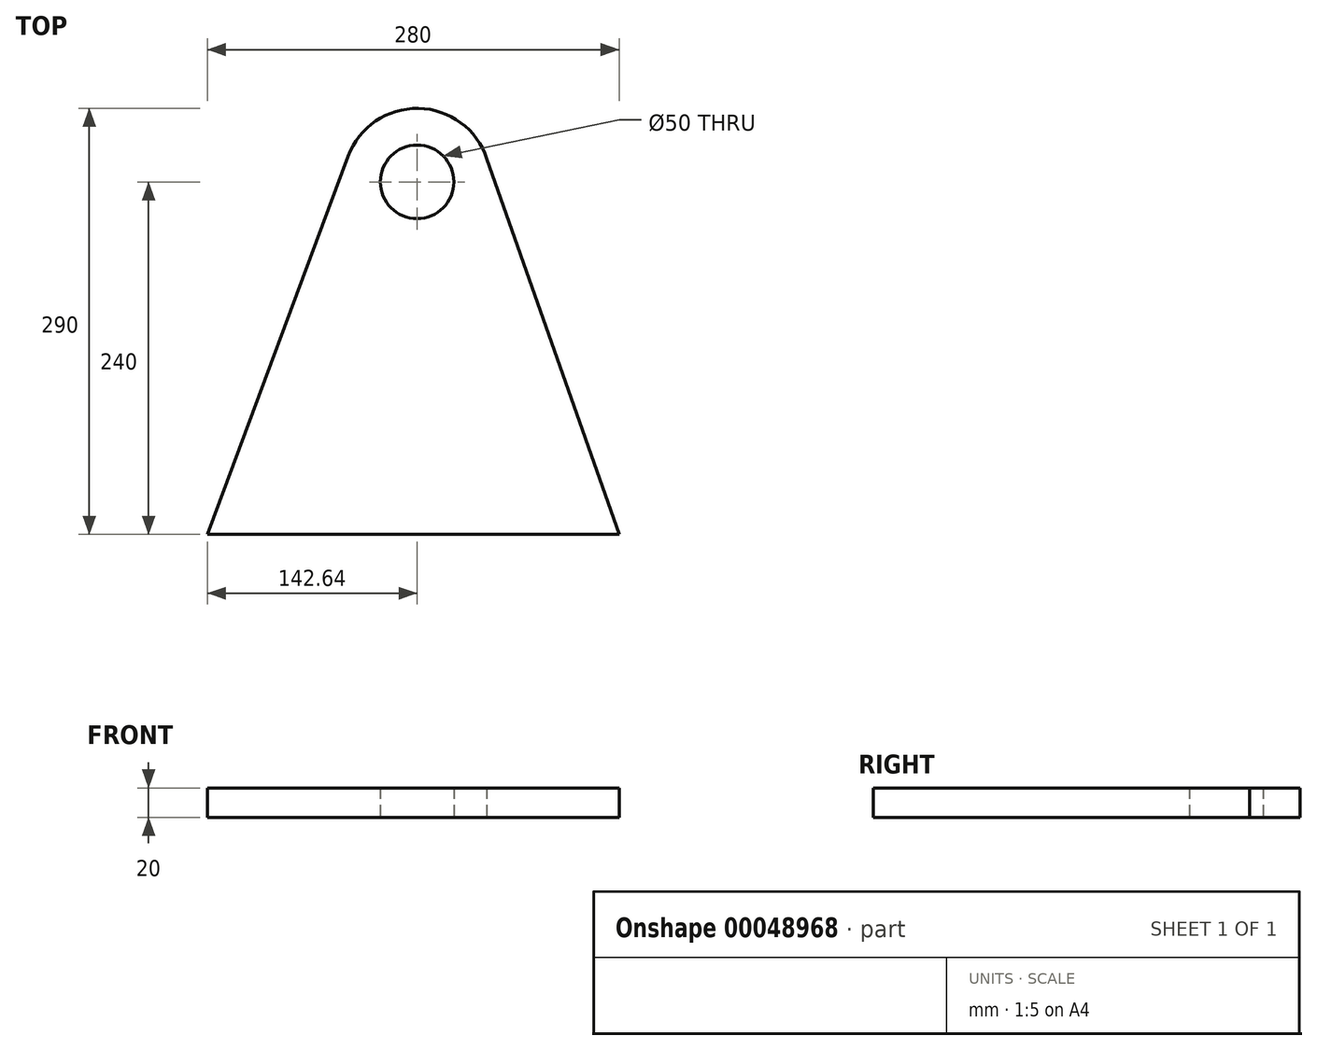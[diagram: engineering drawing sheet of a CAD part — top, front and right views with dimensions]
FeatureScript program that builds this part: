
annotation { "Feature Type Name" : "Feature", "Feature Type Description" : "" }
export const myFeature = defineFeature(function(context is Context, id is Id, definition is map)
    precondition{}
    {
        {
            var Q0;
            Q0=qCreatedBy(makeId("Top.planeOp"),FACE);
            var sketch = newSketch(context, id + "F0", { "sketchPlane" : qUnion([Q0])});
            skLineSegment(sketch, "E0", {"start": v(0, 0) * mm, "end": v(0, 240) * mm, "construction": true});
            skArc(sketch, "E1", {"start": v(47.46, 255.73) * mm, "mid": v(0.9, 290) * mm, "end": v(-46.86, 257.43) * mm});
            skLineSegment(sketch, "E2", {"start": v(46.86, 257.43) * mm, "end": v(137.36, 0) * mm});
            skLineSegment(sketch, "E3", {"start": v(137.36, 0) * mm, "end": v(-142.64, 0) * mm});
            skLineSegment(sketch, "E4", {"start": v(-142.64, 0) * mm, "end": v(-46.86, 257.43) * mm});
            skCircle(sketch, "E5", {"center": v(0, 240) * mm, "radius": 25 * mm});
            skSolve(sketch);
        }
        {
            var Q0;
            Q0 = qSketchRegion(id + "F0", true);
            extrude(context, id + "F1", {"entities" : qUnion([Q0]), "depth" : 20 * mm});
        }
    });
